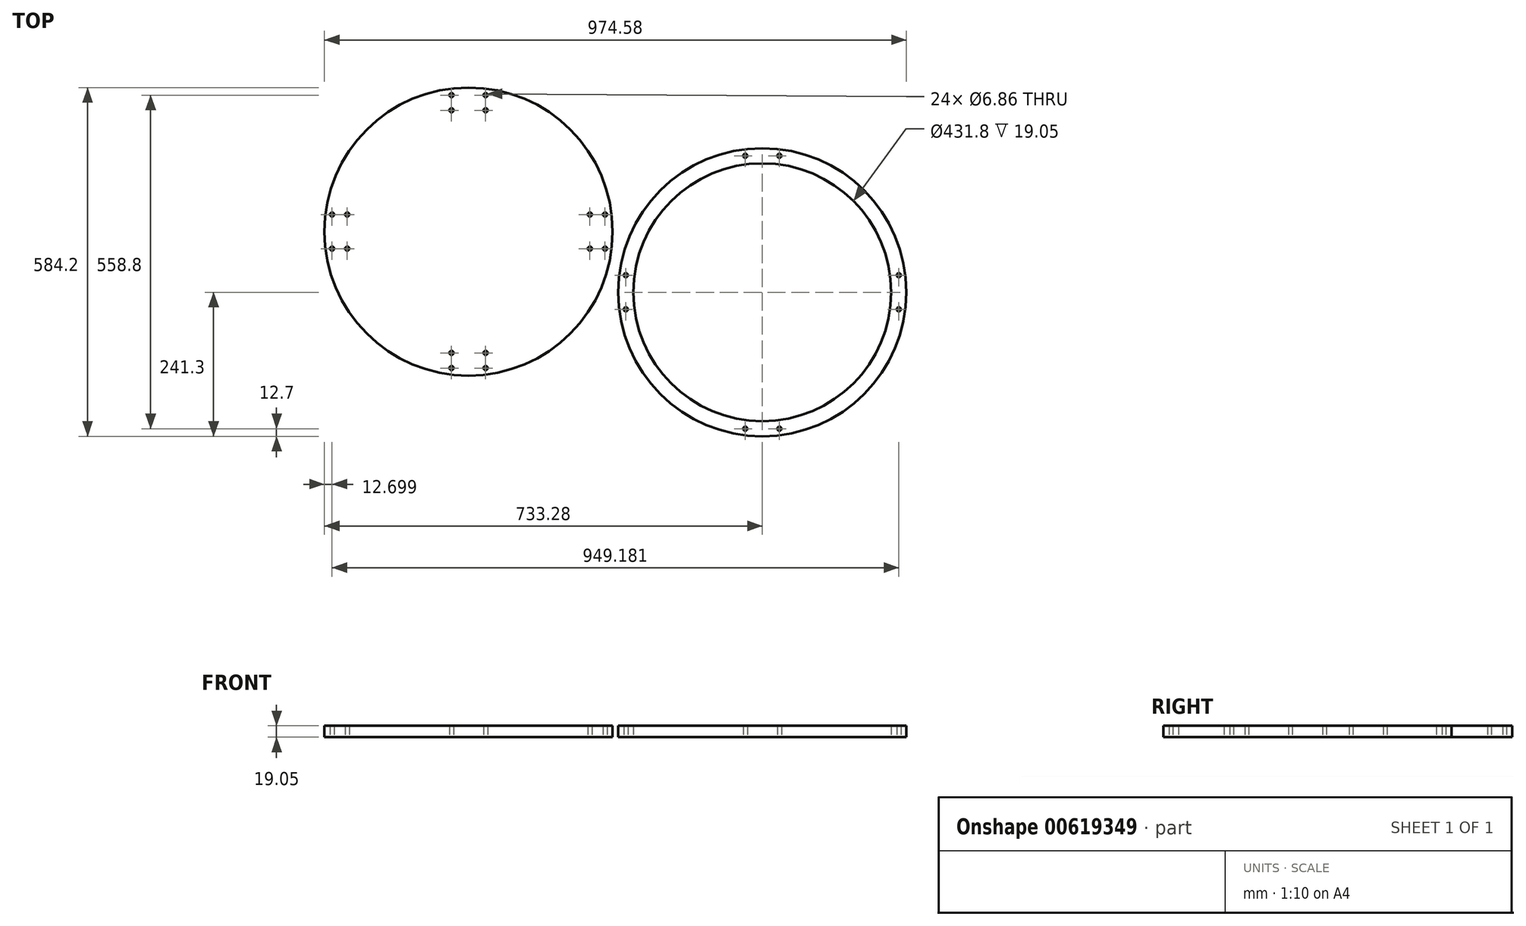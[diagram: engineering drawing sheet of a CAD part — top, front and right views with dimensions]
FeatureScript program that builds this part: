
annotation { "Feature Type Name" : "Feature", "Feature Type Description" : "" }
export const myFeature = defineFeature(function(context is Context, id is Id, definition is map)
    precondition{}
    {
        {
            var Q0;
            Q0=qCreatedBy(makeId("Top.planeOp"),FACE);
            var sketch = newSketch(context, id + "F0", { "sketchPlane" : qUnion([Q0])});
            skCircle(sketch, "E0", {"center": v(0, 0) * mm, "radius": 241.3 * mm});
            skCircle(sketch, "E1", {"center": v(0, 0) * mm, "radius": 215.9 * mm});
            skLineSegment(sketch, "E2", {"start": v(0, 0) * mm, "end": v(0, 341.69) * mm, "construction": true});
            skCircle(sketch, "E3", {"center": v(-491.98, 101.6) * mm, "radius": 241.3 * mm});
            skPoint(sketch, "E4.start.orphan", {"position": v(215.9, 0) * mm});
            skPoint(sketch, "E5.start.orphan", {"position": v(-215.9, 0) * mm});
            skLineSegment(sketch, "E6", {"start": v(-491.98, 101.6) * mm, "end": v(-491.98, 442.01) * mm, "construction": true});
            skCircle(sketch, "E7", {"center": v(-520.56, 330.2) * mm, "radius": 3.43 * mm});
            skCircle(sketch, "E8", {"center": v(-520.56, 304.8) * mm, "radius": 3.43 * mm});
            skCircle(sketch, "E9.MirrorC", {"center": v(-463.4, 330.2) * mm, "radius": 3.43 * mm});
            skCircle(sketch, "E10.MirrorC", {"center": v(-463.4, 304.8) * mm, "radius": 3.43 * mm});
            skLineSegment(sketch, "E11.1.0", {"start": v(-491.98, 101.6) * mm, "end": v(-832.4, 101.6) * mm, "construction": true});
            skCircle(sketch, "E11.1.1", {"center": v(-695.18, 130.17) * mm, "radius": 3.43 * mm});
            skCircle(sketch, "E11.1.2", {"center": v(-695.18, 73.02) * mm, "radius": 3.43 * mm});
            skCircle(sketch, "E11.1.3", {"center": v(-720.58, 130.17) * mm, "radius": 3.43 * mm});
            skCircle(sketch, "E11.1.4", {"center": v(-720.58, 73.02) * mm, "radius": 3.43 * mm});
            skLineSegment(sketch, "E11.2.0", {"start": v(-491.98, 101.6) * mm, "end": v(-491.98, -238.81) * mm, "construction": true});
            skCircle(sketch, "E11.2.1", {"center": v(-520.56, -101.6) * mm, "radius": 3.43 * mm});
            skCircle(sketch, "E11.2.2", {"center": v(-463.4, -101.6) * mm, "radius": 3.43 * mm});
            skCircle(sketch, "E11.2.3", {"center": v(-520.56, -127) * mm, "radius": 3.43 * mm});
            skCircle(sketch, "E11.2.4", {"center": v(-463.4, -127) * mm, "radius": 3.43 * mm});
            skLineSegment(sketch, "E12.1.3.0", {"start": v(-491.98, 101.6) * mm, "end": v(-151.57, 101.6) * mm, "construction": true});
            skCircle(sketch, "E12.3.3.0", {"center": v(-288.78, 73.02) * mm, "radius": 3.43 * mm});
            skCircle(sketch, "E12.5.3.0", {"center": v(-288.78, 130.17) * mm, "radius": 3.43 * mm});
            skCircle(sketch, "E12.7.3.0", {"center": v(-263.38, 73.02) * mm, "radius": 3.43 * mm});
            skCircle(sketch, "E12.9.3.0", {"center": v(-263.38, 130.17) * mm, "radius": 3.43 * mm});
            skLineSegment(sketch, "E13", {"start": v(-132.73, 50.8) * mm, "end": v(-132.73, 342.8) * mm, "construction": true});
            skArc(sketch, "E14", {"start": v(-225.07, 273.73) * mm, "mid": v(-179.8, 287.46) * mm, "end": v(-132.73, 292.1) * mm});
            skArc(sketch, "E15", {"start": v(-225.07, 324.53) * mm, "mid": v(-179.8, 338.26) * mm, "end": v(-132.73, 342.9) * mm});
            skArc(sketch, "E16", {"start": v(-215.35, 250.27) * mm, "mid": v(-174.85, 262.55) * mm, "end": v(-132.73, 266.7) * mm});
            skArc(sketch, "E17", {"start": v(-215.35, 301.07) * mm, "mid": v(-174.85, 313.35) * mm, "end": v(-132.73, 317.5) * mm});
            skLineSegment(sketch, "E18.trimOffspring", {"start": v(-215.35, 250.27) * mm, "end": v(-225.07, 273.73) * mm});
            skLineSegment(sketch, "E19", {"start": v(-215.35, 301.07) * mm, "end": v(-225.07, 324.53) * mm});
            skArc(sketch, "E20.MirrorCS", {"start": v(-40.39, 324.53) * mm, "mid": v(-85.66, 338.26) * mm, "end": v(-132.73, 342.9) * mm});
            skLineSegment(sketch, "E21.MirrorCS", {"start": v(-50.1, 250.27) * mm, "end": v(-40.39, 273.73) * mm});
            skArc(sketch, "E22.MirrorCS", {"start": v(-40.39, 273.73) * mm, "mid": v(-85.66, 287.46) * mm, "end": v(-132.73, 292.1) * mm});
            skArc(sketch, "E23.MirrorCS", {"start": v(-50.1, 250.27) * mm, "mid": v(-90.61, 262.55) * mm, "end": v(-132.73, 266.7) * mm});
            skLineSegment(sketch, "E24.MirrorCS", {"start": v(-50.1, 301.07) * mm, "end": v(-40.39, 324.53) * mm});
            skArc(sketch, "E25.MirrorCS", {"start": v(-50.1, 301.07) * mm, "mid": v(-90.61, 313.35) * mm, "end": v(-132.73, 317.5) * mm});
            skCircle(sketch, "E26", {"center": v(-161.3, 330.2) * mm, "radius": 3.43 * mm});
            skCircle(sketch, "E27", {"center": v(-161.3, 279.4) * mm, "radius": 3.43 * mm});
            skCircle(sketch, "E28.MirrorC", {"center": v(-104.16, 330.2) * mm, "radius": 3.43 * mm});
            skCircle(sketch, "E29.MirrorC", {"center": v(-104.16, 279.4) * mm, "radius": 3.43 * mm});
            skCircle(sketch, "E30", {"center": v(-28.58, 228.6) * mm, "radius": 3.43 * mm});
            skCircle(sketch, "E31.MirrorC", {"center": v(28.58, 228.6) * mm, "radius": 3.43 * mm});
            skCircle(sketch, "E32.1.0", {"center": v(-228.6, -28.57) * mm, "radius": 3.43 * mm});
            skCircle(sketch, "E32.1.1", {"center": v(-228.6, 28.58) * mm, "radius": 3.43 * mm});
            skCircle(sketch, "E32.2.0", {"center": v(28.57, -228.6) * mm, "radius": 3.43 * mm});
            skCircle(sketch, "E32.2.1", {"center": v(-28.58, -228.6) * mm, "radius": 3.43 * mm});
            skCircle(sketch, "E32.3.0", {"center": v(228.6, 28.57) * mm, "radius": 3.43 * mm});
            skCircle(sketch, "E32.3.1", {"center": v(228.6, -28.58) * mm, "radius": 3.43 * mm});
            skLineSegment(sketch, "E33", {"start": v(0, 0) * mm, "end": v(0, -303.1) * mm, "construction": true});
            skArc(sketch, "E34", {"start": v(-92.34, 183.93) * mm, "mid": v(-47.08, 197.66) * mm, "end": v(0, 202.3) * mm});
            skLineSegment(sketch, "E35", {"start": v(0, -39) * mm, "end": v(-92.34, 183.93) * mm, "construction": true});
            skArc(sketch, "E36", {"start": v(-82.62, 160.46) * mm, "mid": v(-42.12, 172.75) * mm, "end": v(0, 176.9) * mm});
            skLineSegment(sketch, "E37", {"start": v(-82.62, 160.46) * mm, "end": v(-92.34, 183.93) * mm});
            skLineSegment(sketch, "E38.MirrorCS", {"start": v(82.62, 160.46) * mm, "end": v(92.34, 183.93) * mm});
            skArc(sketch, "E39.MirrorCS", {"start": v(82.62, 160.46) * mm, "mid": v(42.12, 172.75) * mm, "end": v(0, 176.9) * mm});
            skArc(sketch, "E40.MirrorCS", {"start": v(92.34, 183.93) * mm, "mid": v(47.08, 197.66) * mm, "end": v(0, 202.3) * mm});
            skArc(sketch, "E41.1.0.0", {"start": v(92.34, 116.25) * mm, "mid": v(47.08, 129.98) * mm, "end": v(0, 134.62) * mm});
            skArc(sketch, "E41.1.0.1", {"start": v(-92.34, 116.25) * mm, "mid": v(-47.08, 129.98) * mm, "end": v(0, 134.62) * mm});
            skArc(sketch, "E41.1.0.2", {"start": v(82.62, 92.79) * mm, "mid": v(42.12, 105.07) * mm, "end": v(0, 109.22) * mm});
            skArc(sketch, "E41.1.0.3", {"start": v(-82.62, 92.79) * mm, "mid": v(-42.12, 105.07) * mm, "end": v(0, 109.22) * mm});
            skLineSegment(sketch, "E41.1.0.4", {"start": v(82.62, 92.79) * mm, "end": v(92.34, 116.25) * mm});
            skLineSegment(sketch, "E41.1.0.5", {"start": v(-82.62, 92.79) * mm, "end": v(-92.34, 116.25) * mm});
            skArc(sketch, "E41.2.0.0", {"start": v(92.34, 48.57) * mm, "mid": v(47.08, 62.3) * mm, "end": v(0, 66.94) * mm});
            skArc(sketch, "E41.2.0.1", {"start": v(-92.34, 48.57) * mm, "mid": v(-47.08, 62.3) * mm, "end": v(0, 66.94) * mm});
            skArc(sketch, "E41.2.0.2", {"start": v(82.62, 25.1) * mm, "mid": v(42.12, 37.4) * mm, "end": v(0, 41.54) * mm});
            skArc(sketch, "E41.2.0.3", {"start": v(-82.62, 25.1) * mm, "mid": v(-42.12, 37.4) * mm, "end": v(0, 41.54) * mm});
            skLineSegment(sketch, "E41.2.0.4", {"start": v(82.62, 25.1) * mm, "end": v(92.34, 48.57) * mm});
            skLineSegment(sketch, "E41.2.0.5", {"start": v(-82.62, 25.1) * mm, "end": v(-92.34, 48.57) * mm});
            skArc(sketch, "E41.3.0.0", {"start": v(92.34, -19.1) * mm, "mid": v(47.08, -5.37) * mm, "end": v(0, -0.74) * mm});
            skArc(sketch, "E41.3.0.1", {"start": v(-92.34, -19.1) * mm, "mid": v(-47.08, -5.37) * mm, "end": v(0, -0.74) * mm});
            skArc(sketch, "E41.3.0.2", {"start": v(82.62, -42.57) * mm, "mid": v(42.12, -30.28) * mm, "end": v(0, -26.14) * mm});
            skArc(sketch, "E41.3.0.3", {"start": v(-82.62, -42.57) * mm, "mid": v(-42.12, -30.28) * mm, "end": v(0, -26.14) * mm});
            skLineSegment(sketch, "E41.3.0.4", {"start": v(82.62, -42.57) * mm, "end": v(92.34, -19.1) * mm});
            skLineSegment(sketch, "E41.3.0.5", {"start": v(-82.62, -42.57) * mm, "end": v(-92.34, -19.1) * mm});
            skLineSegment(sketch, "E41.direction1", {"start": v(0, -39) * mm, "end": v(0, -106.68) * mm, "construction": true});
            skSolve(sketch);
        }
        {
            var Q0;
            Q0=makeQuery(id+"F0.imprint","IMPRINT",FACE,{"disambiguationData":[TD([[makeQuery(id+"F0.imprint","IMPRINT",EDGE,{"derivedFrom":sQuery(id+"F0.wireOp",EDGE,"E3")}),1.0]])]});
            var Q1;
            Q1=makeQuery(id+"F0.imprint","IMPRINT",FACE,{"disambiguationData":[TD([[makeQuery(id+"F0.imprint","IMPRINT",EDGE,{"derivedFrom":sQuery(id+"F0.wireOp",EDGE,"E15")}),-1.0]])]});
            var Q2;
            Q2=makeQuery(id+"F0.imprint","IMPRINT",FACE,{"disambiguationData":[TD([[makeQuery(id+"F0.imprint","IMPRINT",EDGE,{"derivedFrom":sQuery(id+"F0.wireOp",EDGE,"10a5b343-3ffb-408e-9a33-fc028350cca11.MirrorCS")}),-1.0]])]});
            var Q3;
            Q3=makeQuery(id+"F0.imprint","IMPRINT",FACE,{"disambiguationData":[TD([[makeQuery(id+"F0.imprint","IMPRINT",EDGE,{"derivedFrom":sQuery(id+"F0.wireOp",EDGE,"10a5b343-3ffb-408e-9a33-fc028350cca10.MirrorCS")}),1.0]])]});
            var Q4;
            Q4=makeQuery(id+"F0.imprint","IMPRINT",FACE,{"disambiguationData":[TD([[makeQuery(id+"F0.imprint","IMPRINT",EDGE,{"derivedFrom":sQuery(id+"F0.wireOp",EDGE,"E14")}),-1.0]])]});
            var Q5;
            Q5=makeQuery(id+"F0.imprint","IMPRINT",FACE,{"disambiguationData":[TD([[makeQuery(id+"F0.imprint","IMPRINT",EDGE,{"derivedFrom":sQuery(id+"F0.wireOp",EDGE,"E0")}),1.0]])]});
            extrude(context, id + "F1", {"entities" : qUnion([Q0, Q1, Q2, Q3, Q4, Q5]), "depth" : 19.05 * mm, "offsetDistance" : 25.4 * mm});
        }
    });
